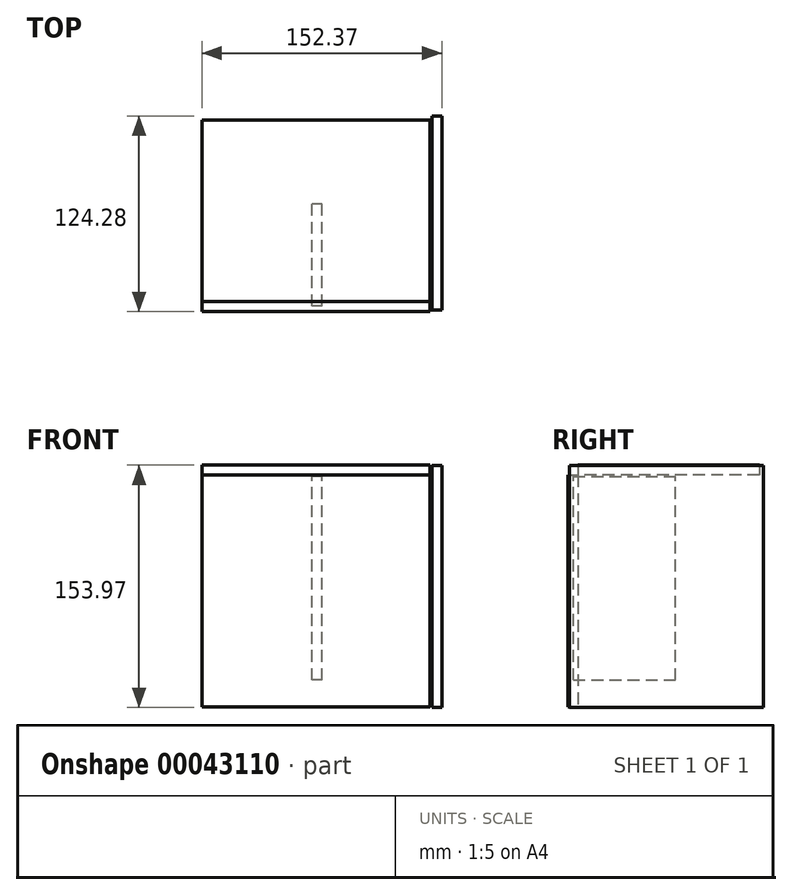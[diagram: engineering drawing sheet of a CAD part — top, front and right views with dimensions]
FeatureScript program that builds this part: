
annotation { "Feature Type Name" : "Feature", "Feature Type Description" : "" }
export const myFeature = defineFeature(function(context is Context, id is Id, definition is map)
    precondition{}
    {
        {
            var Q0;
            Q0=qCreatedBy(makeId("Front.planeOp"),FACE);
            var sketch = newSketch(context, id + "F0", { "sketchPlane" : qUnion([Q0])});
            skLineSegment(sketch, "E0.bottom", {"start": v(-69.82, 72.75) * mm, "end": v(75.07, 72.75) * mm});
            skLineSegment(sketch, "E0.top", {"start": v(-69.82, -74.36) * mm, "end": v(75.07, -74.36) * mm});
            skLineSegment(sketch, "E0.left", {"start": v(-69.82, 72.75) * mm, "end": v(-69.82, -74.36) * mm});
            skLineSegment(sketch, "E0.right", {"start": v(75.07, 72.75) * mm, "end": v(75.07, -74.36) * mm});
            skSolve(sketch);
        }
        {
            var Q0;
            Q0 = qSketchRegion(id + "F0", true);
            extrude(context, id + "F1", {"entities" : qUnion([Q0]), "depth" : 6.35 * mm});
        }
        {
            var Q0;
            Q0=makeQuery(id+"F1.opExtrude","SWEPT_FACE",FACE,{"disambiguationData":[OSD([sQuery(id+"F0.wireOp",EDGE,"E0.bottom")])]});
            var sketch = newSketch(context, id + "F2", { "sketchPlane" : qUnion([Q0])});
            skLineSegment(sketch, "E1.bottom", {"start": v(-69.82, 115.27) * mm, "end": v(75.07, 115.27) * mm});
            skLineSegment(sketch, "E1.top", {"start": v(-69.82, 0) * mm, "end": v(75.07, 0) * mm});
            skLineSegment(sketch, "E1.left", {"start": v(-69.82, 115.27) * mm, "end": v(-69.82, 0) * mm});
            skLineSegment(sketch, "E1.right", {"start": v(75.07, 115.27) * mm, "end": v(75.07, 0) * mm});
            skSolve(sketch);
        }
        {
            var Q0;
            Q0 = qSketchRegion(id + "F2", true);
            extrude(context, id + "F3", {"entities" : qUnion([Q0]), "depth" : 6.35 * mm});
        }
        {
            var Q0;
            Q0=qCreatedBy(makeId("Right.planeOp"),FACE);
            var sketch = newSketch(context, id + "F4", { "sketchPlane" : qUnion([Q0])});
            skLineSegment(sketch, "E2.bottom", {"start": v(-2.86, -57.43) * mm, "end": v(61.92, -57.43) * mm});
            skLineSegment(sketch, "E2.top", {"start": v(-2.86, 71.9) * mm, "end": v(61.92, 71.9) * mm});
            skLineSegment(sketch, "E2.left", {"start": v(-2.86, -57.43) * mm, "end": v(-2.86, 71.9) * mm});
            skLineSegment(sketch, "E2.right", {"start": v(61.92, -57.43) * mm, "end": v(61.92, 71.9) * mm});
            skLineSegment(sketch, "E3.bottom", {"start": v(61.92, 11.82) * mm, "end": v(115.62, 11.82) * mm});
            skLineSegment(sketch, "E3.top", {"start": v(61.92, 71.9) * mm, "end": v(115.62, 71.9) * mm});
            skLineSegment(sketch, "E3.left", {"start": v(61.92, 11.82) * mm, "end": v(61.92, 71.9) * mm});
            skLineSegment(sketch, "E3.right", {"start": v(115.62, 11.82) * mm, "end": v(115.62, 71.9) * mm});
            skSolve(sketch);
        }
        {
            var Q0;
            Q0=makeQuery(id+"F4.imprint","IMPRINT",FACE,{"disambiguationData":[TD([[makeQuery(id+"F4.imprint","IMPRINT",EDGE,{"derivedFrom":sQuery(id+"F4.wireOp",EDGE,"E2.bottom")}),1.0]])]});
            extrude(context, id + "F5", {"entities" : qUnion([Q0]), "depth" : 6.35 * mm});
        }
        {
            var Q0;
            Q0=qCreatedBy(makeId("Right.planeOp"),FACE);
            cPlane(context, id + "F6", {"entities" : qUnion([Q0]), "cplaneType" : CPlaneType.OFFSET, "offset" : 76.2 * mm, "width" : 152.4 * mm, "height" : 152.4 * mm});
        }
        {
            var Q0;
            Q0=qCreatedBy(id+"F6.planeOp",FACE);
            var sketch = newSketch(context, id + "F7", { "sketchPlane" : qUnion([Q0])});
            skLineSegment(sketch, "E4.bottom", {"start": v(-5.35, -74.87) * mm, "end": v(117.93, -74.87) * mm});
            skLineSegment(sketch, "E4.top", {"start": v(-5.35, 79) * mm, "end": v(117.93, 79) * mm});
            skLineSegment(sketch, "E4.left", {"start": v(-5.35, -74.87) * mm, "end": v(-5.35, 79) * mm});
            skLineSegment(sketch, "E4.right", {"start": v(117.93, -74.87) * mm, "end": v(117.93, 79) * mm});
            skSolve(sketch);
        }
        {
            var Q0;
            Q0 = qSketchRegion(id + "F7", true);
            extrude(context, id + "F8", {"entities" : qUnion([Q0]), "depth" : 6.35 * mm});
        }
    });
